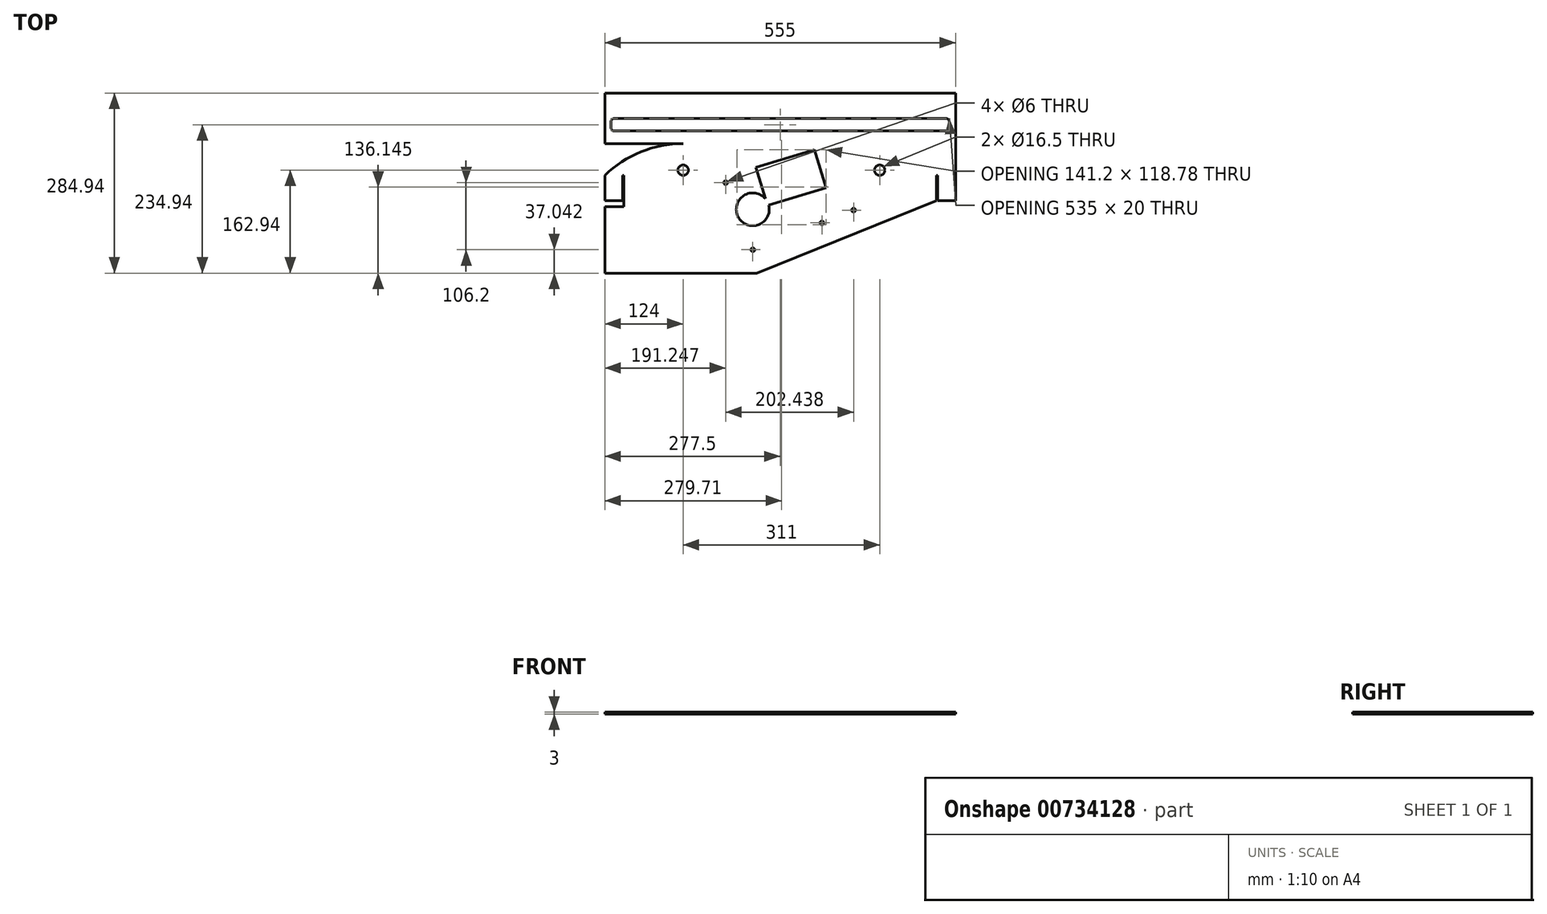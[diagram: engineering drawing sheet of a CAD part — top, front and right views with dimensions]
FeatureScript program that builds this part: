
annotation { "Feature Type Name" : "Feature", "Feature Type Description" : "" }
export const myFeature = defineFeature(function(context is Context, id is Id, definition is map)
    precondition{}
    {
        {
            var Q0;
            Q0=qCreatedBy(makeId("Top.planeOp"),FACE);
            var sketch = newSketch(context, id + "F0", { "sketchPlane" : qUnion([Q0])});
            skCircle(sketch, "E0", {"center": v(-140.75, 30.5) * mm, "radius": 3 * mm});
            skCircle(sketch, "E1", {"center": v(-54.75, 30.5) * mm, "radius": 3 * mm});
            skCircle(sketch, "E2", {"center": v(-97.75, -75.7) * mm, "radius": 3 * mm});
            skCircle(sketch, "E3", {"center": v(-97.75, -11.7) * mm, "radius": 26 * mm});
            skLineSegment(sketch, "E4.top", {"start": v(-92, -112.74) * mm, "end": v(-332, -112.74) * mm});
            skLineSegment(sketch, "E4.right", {"start": v(-302, 42.2) * mm, "end": v(-302, -7.8) * mm});
            skLineSegment(sketch, "E5.trimOffspring", {"start": v(223, 92.2) * mm, "end": v(223, 92.2) * mm});
            skLineSegment(sketch, "E6.top", {"start": v(-302, -7.8) * mm, "end": v(-332, -7.8) * mm});
            skLineSegment(sketch, "E6.right", {"start": v(-332, -112.74) * mm, "end": v(-332, -7.8) * mm});
            skLineSegment(sketch, "E7.trimOffspring", {"start": v(193, 42.2) * mm, "end": v(193, 2.2) * mm});
            skPoint(sketch, "E8.second.point", {"position": v(-332, 42.2) * mm});
            skArc(sketch, "E9", {"start": v(-208, 92.2) * mm, "mid": v(-274.85, 79.23) * mm, "end": v(-332, 42.2) * mm});
            skLineSegment(sketch, "E10.top", {"start": v(-332, 2.2) * mm, "end": v(-304, 2.2) * mm});
            skLineSegment(sketch, "E10.left", {"start": v(-332, 42.2) * mm, "end": v(-332, 2.2) * mm});
            skLineSegment(sketch, "E10.right", {"start": v(-304, 42.2) * mm, "end": v(-304, 2.2) * mm});
            skLineSegment(sketch, "E11.top", {"start": v(223, 2.2) * mm, "end": v(195, 2.2) * mm});
            skLineSegment(sketch, "E11.left", {"start": v(223, 42.2) * mm, "end": v(223, 2.2) * mm});
            skLineSegment(sketch, "E11.right", {"start": v(195, 42.2) * mm, "end": v(195, 2.2) * mm});
            skCircle(sketch, "E12", {"center": v(103, 50.2) * mm, "radius": 8.25 * mm});
            skLineSegment(sketch, "E13", {"start": v(193, 2.2) * mm, "end": v(-92, -112.74) * mm});
            skLineSegment(sketch, "E14", {"start": v(193, 42.2) * mm, "end": v(195, 42.2) * mm});
            skLineSegment(sketch, "E15", {"start": v(-304, 42.2) * mm, "end": v(-302, 42.2) * mm});
            skLineSegment(sketch, "E16", {"start": v(223, 92.2) * mm, "end": v(223, 42.2) * mm});
            skLineSegment(sketch, "E17", {"start": v(-208, 92.2) * mm, "end": v(223, 92.2) * mm});
            skLineSegment(sketch, "E18.bottom", {"start": v(223, 92.2) * mm, "end": v(-332, 92.2) * mm});
            skLineSegment(sketch, "E18.top", {"start": v(223, 172.2) * mm, "end": v(-332, 172.2) * mm});
            skLineSegment(sketch, "E18.left", {"start": v(223, 92.2) * mm, "end": v(223, 172.2) * mm});
            skLineSegment(sketch, "E18.right", {"start": v(-332, 92.2) * mm, "end": v(-332, 172.2) * mm});
            skCircle(sketch, "E19", {"center": v(11.68, -33.19) * mm, "radius": 3 * mm});
            skCircle(sketch, "E20", {"center": v(61.68, -13.02) * mm, "radius": 3 * mm});
            skCircle(sketch, "E21", {"center": v(-208, 50.2) * mm, "radius": 8.25 * mm});
            skCircle(sketch, "E22", {"center": v(-208, 50.2) * mm, "radius": 40 * mm, "construction": true});
            skCircle(sketch, "E23", {"center": v(103, 50.2) * mm, "radius": 40 * mm, "construction": true});
            skCircle(sketch, "E24", {"center": v(-97.75, -11.7) * mm, "radius": 75 * mm, "construction": true});
            skFitSpline(sketch, "E25", {"points": [v(-239.13, 25.08) * mm, v(-127.46, -80.56) * mm, v(-108.76, -85.89) * mm, v(-97.75, -86.7) * mm, v(-73.5, -82.67) * mm, v(-56.39, -74.26) * mm, v(121.84, 14.92) * mm], "startDerivative": vector(438.87, -620.26) * mm, "endDerivative": vector(650.72, 513.51) * mm});
            skLineSegment(sketch, "E26", {"start": v(-208, 90.2) * mm, "end": v(103, 90.2) * mm});
            skLineSegment(sketch, "E27", {"start": v(-317, 132.2) * mm, "end": v(208, 132.2) * mm});
            skLineSegment(sketch, "E28.0", {"start": v(-317, 112.2) * mm, "end": v(208, 112.2) * mm});
            skLineSegment(sketch, "E29", {"start": v(-322, 127.2) * mm, "end": v(-322, 117.2) * mm});
            skLineSegment(sketch, "E30", {"start": v(213, 127.2) * mm, "end": v(213, 117.2) * mm});
            skArc(sketch, "E31.filletArc", {"start": v(-317, 132.2) * mm, "mid": v(-320.54, 130.74) * mm, "end": v(-322, 127.2) * mm});
            skArc(sketch, "E32.filletArc", {"start": v(-322, 117.2) * mm, "mid": v(-320.54, 113.66) * mm, "end": v(-317, 112.2) * mm});
            skArc(sketch, "E33.filletArc", {"start": v(213, 127.2) * mm, "mid": v(211.54, 130.74) * mm, "end": v(208, 132.2) * mm});
            skArc(sketch, "E34.filletArc", {"start": v(208, 112.2) * mm, "mid": v(211.54, 113.66) * mm, "end": v(213, 117.2) * mm});
            skLineSegment(sketch, "E35.bottom", {"start": v(18.31, 22.52) * mm, "end": v(-74.5, -5.68) * mm});
            skLineSegment(sketch, "E35.top", {"start": v(0, 82.8) * mm, "end": v(-92.81, 54.6) * mm});
            skLineSegment(sketch, "E35.left", {"start": v(18.31, 22.52) * mm, "end": v(0, 82.8) * mm});
            skLineSegment(sketch, "E35.right", {"start": v(-74.5, -5.68) * mm, "end": v(-92.81, 54.6) * mm});
            skSolve(sketch);
        }
        {
            var Q0;
            Q0=makeQuery(id+"F0.imprint","IMPRINT",FACE,{"disambiguationData":[TD([[makeQuery(id+"F0.imprint","IMPRINT",EDGE,{"derivedFrom":sQuery(id+"F0.wireOp",EDGE,"E0")}),-1.0]])]});
            extrude(context, id + "F1", {"entities" : qUnion([Q0]), "depth" : 3 * mm});
        }
        {
            var Q0;
            Q0=qSketchRegion(id+"F0",true);
            extrude(context, id + "F2", {"entities" : qUnion([Q0]), "operationType" : NewBodyOperationType.ADD, "depth" : 3 * mm});
        }
    });
